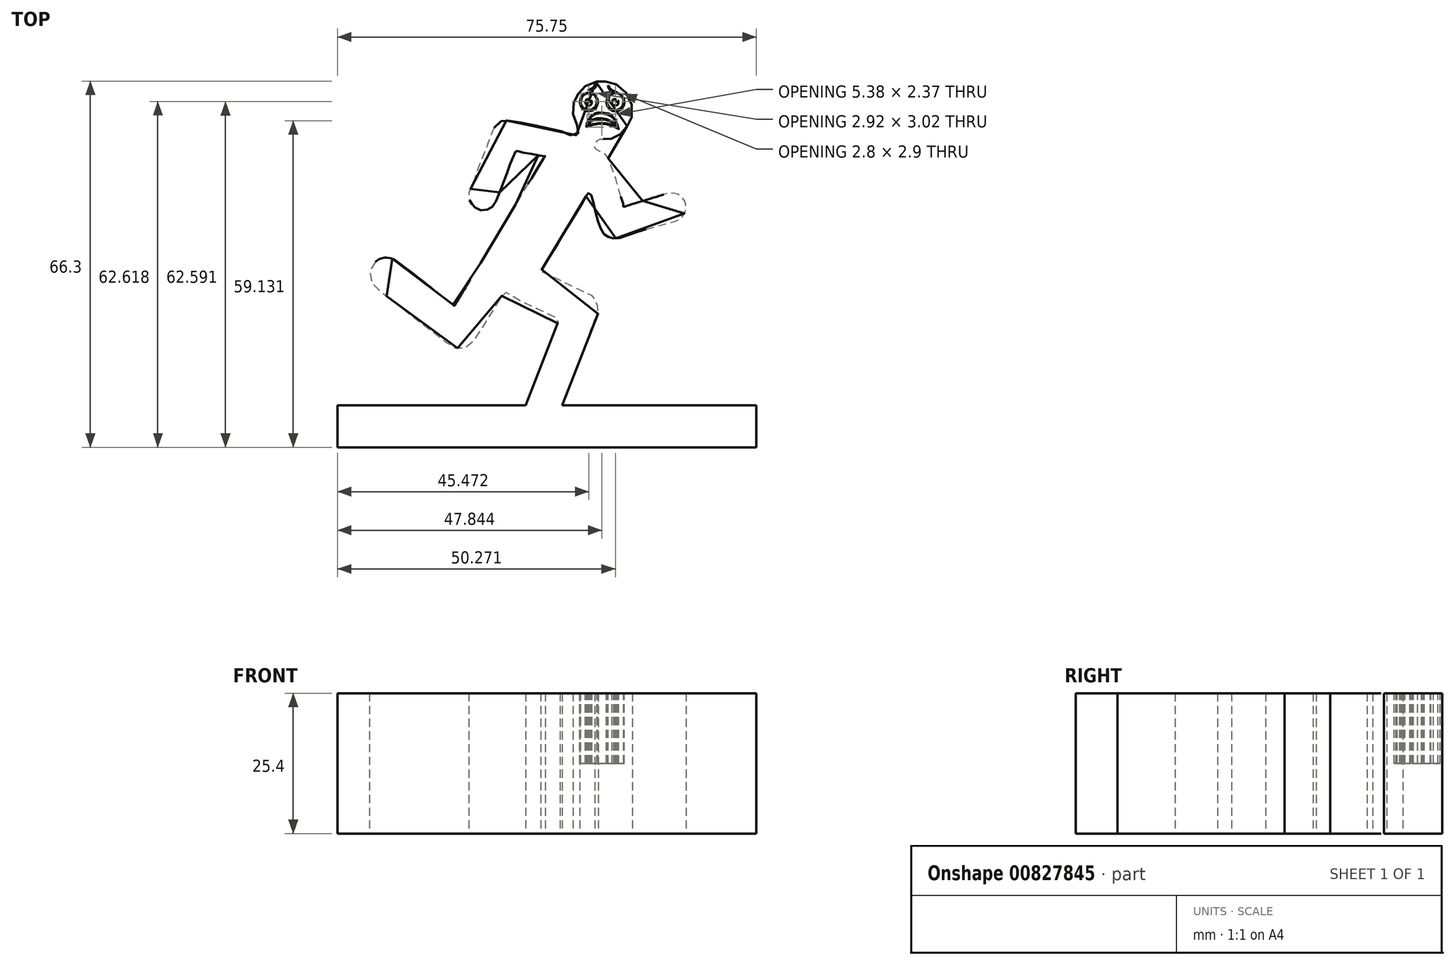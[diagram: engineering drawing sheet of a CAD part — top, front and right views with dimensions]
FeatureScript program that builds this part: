
annotation { "Feature Type Name" : "Feature", "Feature Type Description" : "" }
export const myFeature = defineFeature(function(context is Context, id is Id, definition is map)
    precondition{}
    {
        {
            var Q0;
            Q0=qCreatedBy(makeId("Top.planeOp"),FACE);
            var sketch = newSketch(context, id + "F0", { "sketchPlane" : qUnion([Q0])});
            skFitSpline(sketch, "E0", {"points": [v(-21.66, 59.84) * mm, v(-20.91, 59.98) * mm, v(-19.32, 60.83) * mm, v(-18.1, 62.33) * mm, v(-17.44, 63.5) * mm, v(-17.25, 65.85) * mm, v(-18.42, 68.39) * mm, v(-20.54, 70.03) * mm, v(-22.37, 70.36) * mm, v(-23.35, 70.36) * mm, v(-25.66, 69.52) * mm, v(-27.02, 68.1) * mm, v(-27.72, 66.75) * mm, v(-27.96, 64.91) * mm, v(-27.44, 62.75) * mm, v(-26.74, 61.63) * mm, v(-27.82, 60.36) * mm, v(-28.85, 60.92) * mm, v(-30.21, 61.35) * mm, v(-33.3, 62.05) * mm, v(-36.55, 62.7) * mm, v(-39.08, 63.18) * mm, v(-40.07, 63.27) * mm, v(-41.48, 62.85) * mm, v(-42.47, 61.44) * mm, v(-43.69, 58.1) * mm, v(-45.1, 54.63) * mm, v(-46.27, 51.34) * mm, v(-46.7, 50.42) * mm, v(-46.73, 49.09) * mm, v(-46.3, 48.26) * mm, v(-45.96, 47.8) * mm, v(-44.73, 47.06) * mm, v(-43.21, 47.25) * mm, v(-42.25, 48) * mm, v(-41.43, 49.73) * mm, v(-40.79, 51.4) * mm, v(-39.83, 53.95) * mm, v(-38.86, 56.52) * mm, v(-38.35, 57.68) * mm, v(-38.28, 57.8) * mm, v(-37.32, 57.53) * mm, v(-35.26, 57.2) * mm, v(-33.07, 56.8) * mm, v(-32.94, 56.82) * mm, v(-33.18, 56.56) * mm, v(-34.23, 54.85) * mm, v(-35.45, 52.79) * mm, v(-36.37, 51.35) * mm, v(-37.5, 49.42) * mm, v(-38.56, 47.69) * mm, v(-40.22, 44.91) * mm, v(-41.6, 42.65) * mm, v(-42.95, 40.41) * mm, v(-43.66, 39.23) * mm, v(-43.85, 38.47) * mm, v(-44.5, 37.76) * mm, v(-44.7, 37.36) * mm, v(-45, 37.08) * mm, v(-45.41, 36.36) * mm, v(-45.84, 35.58) * mm, v(-46.74, 34.1) * mm, v(-47.46, 32.89) * mm, v(-48.92, 30.49) * mm, v(-49.28, 29.87) * mm, v(-49.37, 29.72) * mm, v(-49.56, 29.9) * mm, v(-50.66, 30.7) * mm, v(-51.77, 31.6) * mm, v(-52.13, 31.84) * mm, v(-56.34, 35.15) * mm, v(-58.68, 36.93) * mm, v(-60.23, 38.05) * mm, v(-61.27, 38.4) * mm, v(-62.8, 38.25) * mm, v(-64, 37.36) * mm, v(-64.53, 36.45) * mm, v(-64.76, 35.3) * mm, v(-64.25, 33.67) * mm, v(-63.39, 32.78) * mm, v(-60.46, 30.57) * mm, v(-57.79, 28.45) * mm, v(-52.78, 24.64) * mm, v(-50.75, 23.02) * mm, v(-49.63, 22.27) * mm, v(-48.82, 22.07) * mm, v(-47.75, 22.07) * mm, v(-46.53, 22.62) * mm, v(-45.2, 24.35) * mm, v(-43.24, 27.48) * mm, v(-42.08, 29.44) * mm, v(-40.94, 31.3) * mm, v(-40.38, 32.3) * mm, v(-40.1, 32.18) * mm, v(-37.91, 30.91) * mm, v(-34.47, 29.25) * mm, v(-30.79, 27.5) * mm, v(-30.3, 27.28) * mm, v(-30.5, 27.02) * mm, v(-30.93, 25.86) * mm, v(-31.9, 23.63) * mm, v(-33.86, 18.47) * mm, v(-35.24, 14.87) * mm, v(-36.02, 12.83) * mm, v(-36.9, 10.73) * mm, v(-37.09, 9.45) * mm, v(-36.65, 8.06) * mm, v(-35.4, 6.8) * mm, v(-33.76, 6.56) * mm, v(-32.34, 7.02) * mm, v(-31.22, 8.25) * mm, v(-30.98, 8.9) * mm, v(-29.97, 11.44) * mm, v(-28.85, 14.36) * mm, v(-28, 16.63) * mm, v(-25.23, 23.8) * mm, v(-23.73, 27.8) * mm, v(-23.4, 28.32) * mm, v(-23.57, 29.95) * mm, v(-24.33, 31.41) * mm, v(-25.52, 32.04) * mm, v(-30.79, 34.57) * mm, v(-33.64, 35.9) * mm, v(-33.78, 36) * mm, v(-33.08, 37) * mm, v(-32.78, 37.64) * mm, v(-31.43, 39.75) * mm, v(-30.22, 41.85) * mm, v(-27.87, 45.7) * mm, v(-25.45, 49.79) * mm, v(-25.2, 50.1) * mm, v(-24.82, 50) * mm, v(-24.03, 47.3) * mm, v(-23.03, 43.89) * mm, v(-22.7, 43.28) * mm, v(-22.42, 42.83) * mm, v(-21.4, 42.13) * mm, v(-20.03, 41.92) * mm, v(-16.7, 42.98) * mm, v(-12.83, 44.1) * mm, v(-10.62, 44.73) * mm, v(-9.1, 45.16) * mm, v(-8.45, 45.55) * mm, v(-7.87, 46.3) * mm, v(-7.5, 47.46) * mm, v(-7.9, 48.96) * mm, v(-8.73, 49.75) * mm, v(-9.67, 50.1) * mm, v(-10.82, 50.1) * mm, v(-11.37, 49.92) * mm, v(-13.83, 49.16) * mm, v(-15.96, 48.53) * mm, v(-18.47, 47.7) * mm, v(-18.78, 47.64) * mm, v(-18.89, 48.2) * mm, v(-19.29, 49.43) * mm, v(-20.05, 52.23) * mm, v(-21.28, 55.73) * mm, v(-21.8, 56.77) * mm, v(-22.9, 57.61) * mm, v(-23.94, 58.32) * mm, v(-23.36, 59.75) * mm, v(-21.66, 59.84) * mm]});
            skSolve(sketch);
        }
        {
            var Q0;
            Q0=makeQuery(id+"F0.imprint","IMPRINT",FACE,{"disambiguationData":[TD([[makeQuery(id+"F0.imprint","IMPRINT",EDGE,{"derivedFrom":sQuery(id+"F0.wireOp",EDGE,"E0")}),1.0]])]});
            extrude(context, id + "F1", {"entities" : qUnion([Q0]), "depth" : 25.4 * mm, "offsetDistance" : 25.4 * mm});
        }
        {
            var Q0;
            Q0=makeQuery(id+"F1.opExtrude","CAP_FACE",FACE,{"disambiguationData":[OSD([sQuery(id+"F0.wireOp",EDGE,"E0")])],"isStart":false});
            var sketch = newSketch(context, id + "F2", { "sketchPlane" : qUnion([Q0])});
            skFitSpline(sketch, "E1", {"points": [v(-24.64, 68.83) * mm, v(-24.44, 68.87) * mm, v(-24.2, 69) * mm, v(-23.93, 69.2) * mm, v(-23.73, 69.53) * mm, v(-23.63, 69.8) * mm, v(-23.61, 69.97) * mm, v(-23.62, 70) * mm, v(-23.63, 70) * mm, v(-23.65, 69.92) * mm, v(-23.73, 69.8) * mm, v(-23.84, 69.67) * mm, v(-23.91, 69.57) * mm, v(-24.14, 69.32) * mm, v(-24.37, 69.15) * mm, v(-24.73, 68.96) * mm, v(-25.04, 68.86) * mm, v(-25.18, 68.82) * mm, v(-24.95, 68.81) * mm, v(-24.64, 68.83) * mm]});
            skFitSpline(sketch, "E2", {"points": [v(-21.55, 69.6) * mm, v(-21.57, 69.54) * mm, v(-21.57, 69.4) * mm, v(-21.5, 69.17) * mm, v(-21.35, 68.9) * mm, v(-21.11, 68.66) * mm, v(-20.79, 68.47) * mm, v(-20.44, 68.37) * mm, v(-20.1, 68.34) * mm, v(-19.95, 68.34) * mm, v(-20.15, 68.44) * mm, v(-20.49, 68.58) * mm, v(-20.85, 68.76) * mm, v(-21.14, 69) * mm, v(-21.38, 69.28) * mm, v(-21.55, 69.6) * mm]});
            skFitSpline(sketch, "E3", {"points": [v(-20.11, 67.13) * mm, v(-20.2, 67.06) * mm, v(-20.26, 66.95) * mm, v(-20.24, 66.77) * mm, v(-20.1, 66.65) * mm, v(-19.96, 66.64) * mm, v(-19.86, 66.66) * mm, v(-19.75, 66.82) * mm, v(-19.73, 66.85) * mm, v(-19.7, 66.65) * mm, v(-19.7, 66.48) * mm, v(-19.79, 66.25) * mm, v(-19.95, 66.05) * mm, v(-20.3, 65.97) * mm, v(-20.6, 66.05) * mm, v(-20.8, 66.22) * mm, v(-20.9, 66.46) * mm, v(-20.86, 66.77) * mm, v(-20.7, 67.01) * mm, v(-20.33, 67.17) * mm, v(-20.11, 67.13) * mm]});
            skFitSpline(sketch, "E4", {"points": [v(-24.9, 67.14) * mm, v(-25, 67.07) * mm, v(-25.05, 67) * mm, v(-25.07, 66.87) * mm, v(-25.06, 66.8) * mm, v(-24.98, 66.7) * mm, v(-24.92, 66.64) * mm, v(-24.72, 66.64) * mm, v(-24.61, 66.74) * mm, v(-24.58, 66.87) * mm, v(-24.55, 66.8) * mm, v(-24.52, 66.6) * mm, v(-24.54, 66.35) * mm, v(-24.64, 66.19) * mm, v(-24.76, 66.07) * mm, v(-25, 65.98) * mm, v(-25.28, 65.99) * mm, v(-25.52, 66.12) * mm, v(-25.7, 66.37) * mm, v(-25.7, 66.65) * mm, v(-25.67, 66.81) * mm, v(-25.52, 67.02) * mm, v(-25.38, 67.1) * mm, v(-25.26, 67.14) * mm, v(-25, 67.16) * mm, v(-24.9, 67.14) * mm]});
            skFitSpline(sketch, "E5", {"points": [v(-25.39, 62.25) * mm, v(-25.38, 62.38) * mm, v(-25.28, 62.67) * mm, v(-25.16, 62.98) * mm, v(-25, 63.35) * mm, v(-24.66, 63.83) * mm, v(-24.31, 64.15) * mm, v(-24, 64.34) * mm, v(-23.6, 64.48) * mm, v(-22.98, 64.56) * mm, v(-22, 64.43) * mm, v(-21.47, 64.27) * mm, v(-20.93, 63.95) * mm, v(-20.38, 63.32) * mm, v(-20.1, 62.67) * mm, v(-19.93, 62.1) * mm, v(-19.95, 62.02) * mm, v(-20.04, 62.07) * mm, v(-20.37, 62.27) * mm, v(-20.93, 62.48) * mm, v(-21.66, 62.68) * mm, v(-22.38, 62.77) * mm, v(-23.17, 62.8) * mm, v(-24.2, 62.66) * mm, v(-24.89, 62.45) * mm, v(-25.39, 62.25) * mm]});
            skFitSpline(sketch, "E6", {"points": [v(-25.53, 62.05) * mm, v(-25.3, 62.14) * mm, v(-24.78, 62.35) * mm, v(-24.07, 62.54) * mm, v(-23.3, 62.66) * mm, v(-22.53, 62.67) * mm, v(-21.81, 62.58) * mm, v(-21.17, 62.4) * mm, v(-20.78, 62.27) * mm, v(-20.2, 62.03) * mm, v(-19.83, 61.82) * mm, v(-19.66, 61.68) * mm, v(-19.69, 61.73) * mm, v(-19.74, 61.86) * mm, v(-19.85, 62.23) * mm, v(-19.93, 62.48) * mm, v(-20.1, 63.08) * mm, v(-20.52, 63.72) * mm, v(-21.4, 64.44) * mm, v(-22.46, 64.69) * mm, v(-23.56, 64.69) * mm, v(-24.36, 64.32) * mm, v(-25.1, 63.54) * mm, v(-25.49, 62.47) * mm, v(-25.53, 62.05) * mm]});
            skFitSpline(sketch, "E7", {"points": [v(-25.37, 62.29) * mm, v(-25.32, 62.47) * mm, v(-25.23, 62.75) * mm, v(-25.12, 63.05) * mm, v(-24.97, 63.36) * mm, v(-24.93, 63.42) * mm, v(-24.88, 63.33) * mm, v(-24.75, 63.14) * mm, v(-24.77, 63.04) * mm, v(-24.9, 62.71) * mm, v(-25.04, 62.41) * mm, v(-25.1, 62.37) * mm, v(-25.31, 62.3) * mm, v(-25.37, 62.29) * mm]});
            skFitSpline(sketch, "E8", {"points": [v(-20.54, 62.7) * mm, v(-20.57, 62.42) * mm, v(-20.57, 62.38) * mm, v(-20.36, 62.3) * mm, v(-20.2, 62.2) * mm, v(-19.98, 62.08) * mm, v(-19.99, 62.2) * mm, v(-20.07, 62.44) * mm, v(-20.16, 62.71) * mm, v(-20.21, 62.88) * mm, v(-20.26, 62.9) * mm, v(-20.4, 62.79) * mm, v(-20.54, 62.7) * mm]});
            skFitSpline(sketch, "E9", {"points": [v(-20.53, 62.79) * mm, v(-20.92, 63.06) * mm, v(-21.6, 63.4) * mm, v(-22.27, 63.59) * mm, v(-22.9, 63.66) * mm, v(-24, 63.54) * mm, v(-24.69, 63.2) * mm, v(-24.62, 63.13) * mm, v(-24.36, 63.27) * mm, v(-23.87, 63.41) * mm, v(-23.1, 63.54) * mm, v(-22.31, 63.48) * mm, v(-21.59, 63.25) * mm, v(-20.78, 62.87) * mm, v(-20.58, 62.73) * mm, v(-20.53, 62.77) * mm, v(-20.53, 62.79) * mm]});
            skFitSpline(sketch, "E10", {"points": [v(-26.34, 65.58) * mm, v(-26.14, 65.31) * mm, v(-25.52, 64.97) * mm, v(-24.76, 64.96) * mm, v(-24.06, 65.27) * mm, v(-23.49, 66.2) * mm, v(-23.49, 67.17) * mm, v(-24.03, 67.92) * mm, v(-24.22, 68.05) * mm, v(-24.55, 68.24) * mm, v(-25.03, 68.3) * mm, v(-25.34, 68.29) * mm, v(-25.94, 68.09) * mm, v(-26.3, 67.71) * mm, v(-26.52, 67.39) * mm, v(-26.7, 66.74) * mm, v(-26.6, 66.11) * mm, v(-26.34, 65.58) * mm]});
            skFitSpline(sketch, "E11", {"points": [v(-21.81, 66.16) * mm, v(-21.87, 66.44) * mm, v(-21.87, 66.74) * mm, v(-21.8, 67.11) * mm, v(-21.64, 67.48) * mm, v(-21.43, 67.8) * mm, v(-20.95, 68.14) * mm, v(-20.67, 68.26) * mm, v(-20.42, 68.3) * mm, v(-20.06, 68.28) * mm, v(-19.65, 68.17) * mm, v(-19.16, 67.86) * mm, v(-18.86, 67.44) * mm, v(-18.7, 67.05) * mm, v(-18.64, 66.56) * mm, v(-18.67, 66.27) * mm, v(-18.83, 65.82) * mm, v(-19.09, 65.46) * mm, v(-19.51, 65.1) * mm, v(-19.95, 64.95) * mm, v(-20.36, 64.91) * mm, v(-21, 65.1) * mm, v(-21.43, 65.47) * mm, v(-21.81, 66.16) * mm]});
            skFitSpline(sketch, "E12", {"points": [v(-20.85, 65.27) * mm, v(-20.45, 65.19) * mm, v(-19.98, 65.17) * mm, v(-19.4, 65.44) * mm, v(-19.04, 65.85) * mm, v(-18.83, 66.36) * mm, v(-18.8, 66.87) * mm, v(-18.93, 67.33) * mm, v(-19.15, 67.7) * mm, v(-19.4, 67.95) * mm, v(-19.86, 68.17) * mm, v(-20.24, 68.23) * mm, v(-20.38, 68.22) * mm, v(-20.67, 68.16) * mm, v(-20.97, 68.03) * mm, v(-21.31, 67.75) * mm, v(-21.64, 67.27) * mm, v(-21.72, 66.65) * mm, v(-21.64, 66.13) * mm, v(-21.35, 65.67) * mm, v(-20.85, 65.27) * mm]});
            skFitSpline(sketch, "E13", {"points": [v(-26.2, 67.67) * mm, v(-26.36, 67.44) * mm, v(-26.51, 66.9) * mm, v(-26.49, 66.3) * mm, v(-26.3, 65.85) * mm, v(-25.91, 65.44) * mm, v(-25.7, 65.32) * mm, v(-25.5, 65.23) * mm, v(-25.15, 65.16) * mm, v(-24.45, 65.3) * mm, v(-23.86, 65.83) * mm, v(-23.65, 66.38) * mm, v(-23.65, 67.13) * mm, v(-24.04, 67.8) * mm, v(-24.54, 68.14) * mm, v(-24.96, 68.21) * mm, v(-25.36, 68.18) * mm, v(-25.91, 67.97) * mm, v(-26.2, 67.67) * mm]});
            skSolve(sketch);
        }
        {
            var Q0;
            Q0=makeQuery(id+"F2.imprint","IMPRINT",FACE,{"disambiguationData":[TD([[makeQuery(id+"F2.imprint","IMPRINT",EDGE,{"derivedFrom":sQuery(id+"F2.wireOp",EDGE,"E10")}),1.0]])]});
            var Q1;
            Q1=makeQuery(id+"F2.imprint","IMPRINT",FACE,{"disambiguationData":[TD([[makeQuery(id+"F2.imprint","IMPRINT",EDGE,{"derivedFrom":sQuery(id+"F2.wireOp",EDGE,"E4")}),-1.0]])]});
            var Q2;
            Q2=makeQuery(id+"F2.imprint","IMPRINT",FACE,{"disambiguationData":[TD([[makeQuery(id+"F2.imprint","IMPRINT",EDGE,{"derivedFrom":sQuery(id+"F2.wireOp",EDGE,"E1")}),1.0]])]});
            var Q3;
            Q3=makeQuery(id+"F2.imprint","IMPRINT",FACE,{"disambiguationData":[TD([[makeQuery(id+"F2.imprint","IMPRINT",EDGE,{"derivedFrom":sQuery(id+"F2.wireOp",EDGE,"E2")}),1.0]])]});
            var Q4;
            Q4=makeQuery(id+"F2.imprint","IMPRINT",FACE,{"disambiguationData":[TD([[makeQuery(id+"F2.imprint","IMPRINT",EDGE,{"derivedFrom":sQuery(id+"F2.wireOp",EDGE,"E11")}),-1.0]])]});
            var Q5;
            Q5=makeQuery(id+"F2.imprint","IMPRINT",FACE,{"disambiguationData":[TD([[makeQuery(id+"F2.imprint","IMPRINT",EDGE,{"derivedFrom":sQuery(id+"F2.wireOp",EDGE,"E3")}),-1.0]])]});
            var Q6;
            Q6=makeQuery(id+"F2.imprint","IMPRINT",FACE,{"disambiguationData":[TD([[makeQuery(id+"F2.imprint","IMPRINT",EDGE,{"derivedFrom":sQuery(id+"F2.wireOp",EDGE,"E7")}),-1.0]])]});
            var Q7;
            Q7=makeQuery(id+"F2.imprint","IMPRINT",FACE,{"disambiguationData":[TD([[makeQuery(id+"F2.imprint","IMPRINT",EDGE,{"derivedFrom":sQuery(id+"F2.wireOp",EDGE,"E8")}),1.0]])]});
            var Q8;
            Q8=makeQuery(id+"F2.imprint","IMPRINT",FACE,{"disambiguationData":[TD([[makeQuery(id+"F2.imprint","IMPRINT",EDGE,{"derivedFrom":sQuery(id+"F2.wireOp",EDGE,"E5")}),1.0]])]});
            var Q9;
            Q9=makeQuery(id+"F2.imprint","IMPRINT",FACE,{"disambiguationData":[TD([[makeQuery(id+"F2.imprint","IMPRINT",EDGE,{"derivedFrom":sQuery(id+"F2.wireOp",EDGE,"E9")}),1.0]])]});
            extrude(context, id + "F3", {"entities" : qUnion([Q0, Q1, Q2, Q3, Q4, Q5, Q6, Q7, Q8, Q9]), "oppositeDirection" : true, "depth" : 12.7 * mm, "offsetDistance" : 25.4 * mm});
        }
        {
            var Q0;
            Q0=qCreatedBy(makeId("Top.planeOp"),FACE);
            var sketch = newSketch(context, id + "F4", { "sketchPlane" : qUnion([Q0])});
            skLineSegment(sketch, "E14.bottom", {"start": v(-70.54, 4.1) * mm, "end": v(5.2, 4.1) * mm});
            skLineSegment(sketch, "E14.top", {"start": v(-70.54, 11.68) * mm, "end": v(5.2, 11.68) * mm});
            skLineSegment(sketch, "E14.left", {"start": v(-70.54, 4.1) * mm, "end": v(-70.54, 11.68) * mm});
            skLineSegment(sketch, "E14.right", {"start": v(5.2, 4.1) * mm, "end": v(5.2, 11.68) * mm});
            skSolve(sketch);
        }
        {
            var Q0;
            Q0=makeQuery(id+"F4.imprint","IMPRINT",FACE,{"disambiguationData":[TD([[makeQuery(id+"F4.imprint","IMPRINT",EDGE,{"derivedFrom":sQuery(id+"F4.wireOp",EDGE,"E14.bottom")}),1.0]])]});
            extrude(context, id + "F5", {"entities" : qUnion([Q0]), "operationType" : NewBodyOperationType.ADD, "depth" : 25.4 * mm, "offsetDistance" : 25.4 * mm});
        }
    });
